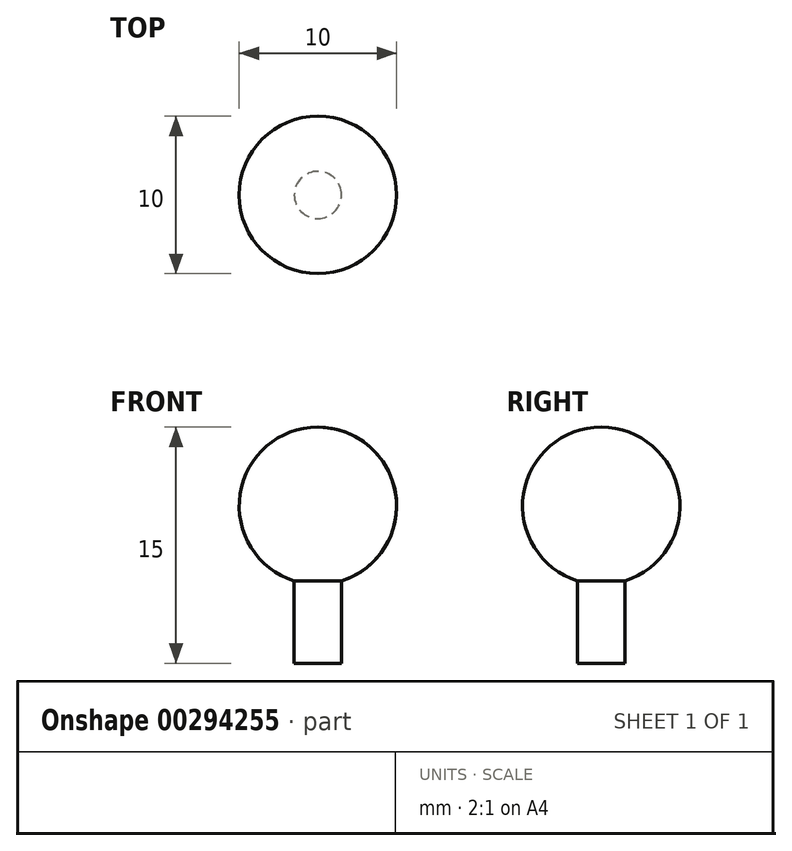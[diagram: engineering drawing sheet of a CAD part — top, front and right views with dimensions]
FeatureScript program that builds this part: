
annotation { "Feature Type Name" : "Feature", "Feature Type Description" : "" }
export const myFeature = defineFeature(function(context is Context, id is Id, definition is map)
    precondition{}
    {
        {
            var Q0;
            Q0=qCreatedBy(makeId("Front.planeOp"),FACE);
            var sketch = newSketch(context, id + "F0", { "sketchPlane" : qUnion([Q0])});
            skArc(sketch, "E0", {"start": v(1.5, -4.77) * mm, "mid": v(4.94, 0.76) * mm, "end": v(0, 5) * mm});
            skLineSegment(sketch, "E1.top", {"start": v(0, -10) * mm, "end": v(1.5, -10) * mm});
            skLineSegment(sketch, "E1.right", {"start": v(1.5, -4.77) * mm, "end": v(1.5, -10) * mm});
            skPoint(sketch, "E2.orphan", {"position": v(-1.5, 10) * mm});
            skPoint(sketch, "E3.orphan", {"position": v(1.5, 10) * mm});
            skLineSegment(sketch, "E4", {"start": v(0, 5) * mm, "end": v(0, -10) * mm});
            skPoint(sketch, "E5.orphan", {"position": v(-1.5, -10) * mm});
            skSolve(sketch);
        }
        {
            var Q0;
            Q0 = qSketchRegion(id + "F0", true);
            var Q1;
            Q1=sQuery(id+"F0.wireOp",EDGE,"E4");
            revolve(context, id + "F1", {"entities" : qUnion([Q0]), "axis" : qUnion([Q1]), "revolveType" : RevolveType.FULL});
        }
    });
